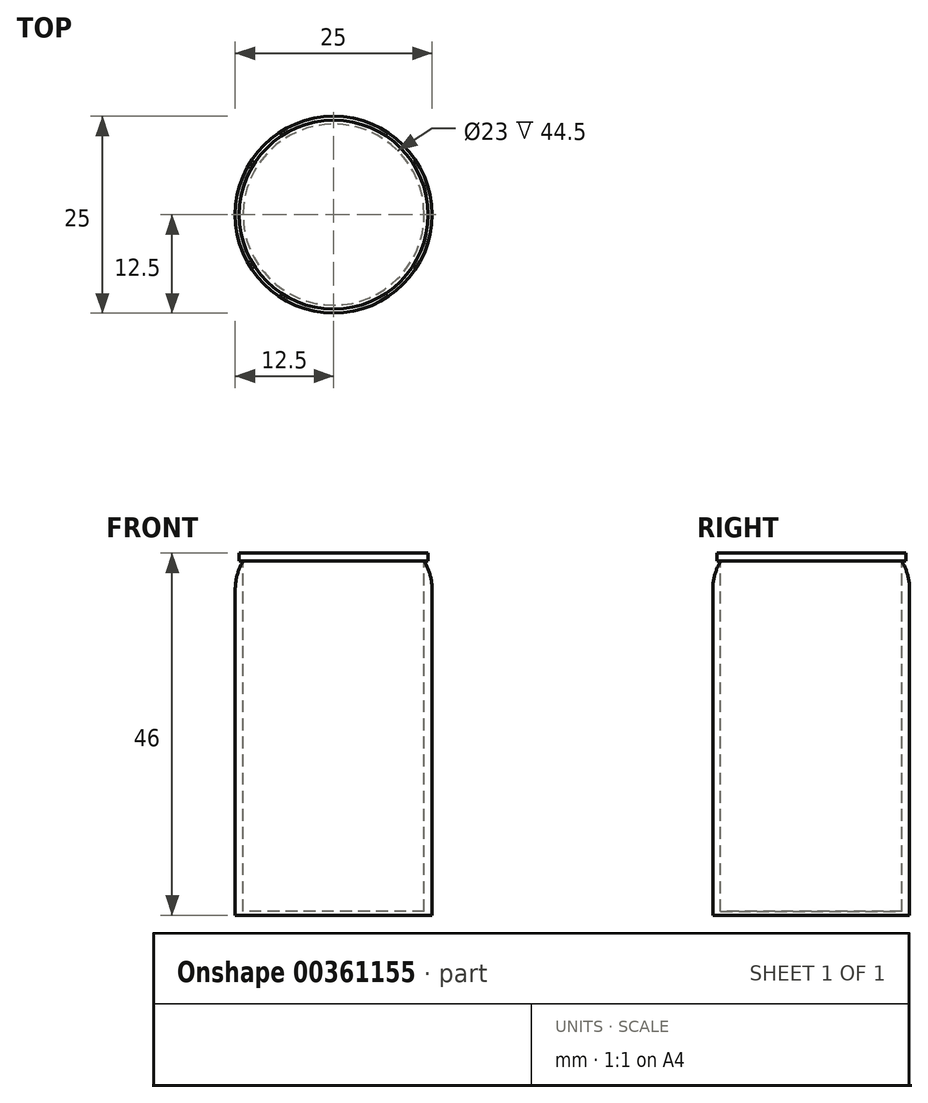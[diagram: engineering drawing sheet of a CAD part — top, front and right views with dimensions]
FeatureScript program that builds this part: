
annotation { "Feature Type Name" : "Feature", "Feature Type Description" : "" }
export const myFeature = defineFeature(function(context is Context, id is Id, definition is map)
    precondition{}
    {
        {
            var Q0;
            Q0=qCreatedBy(makeId("Top.planeOp"),FACE);
            var sketch = newSketch(context, id + "F0", { "sketchPlane" : qUnion([Q0])});
            skCircle(sketch, "E0", {"center": v(0, 0) * mm, "radius": 12.5 * mm});
            skSolve(sketch);
        }
        {
            var Q0;
            Q0 = qSketchRegion(id + "F0", true);
            extrude(context, id + "F1", {"entities" : qUnion([Q0]), "depth" : 45 * mm});
        }
        {
            var Q0;
            Q0=makeQuery(id+"F1.opExtrude","CAP_FACE",FACE,{"disambiguationData":[OSD([sQuery(id+"F0.wireOp",EDGE,"E0")])],"isStart":false});
            var sketch = newSketch(context, id + "F2", { "sketchPlane" : qUnion([Q0])});
            skCircle(sketch, "E1", {"center": v(0, 0) * mm, "radius": 6.5 * mm});
            skSolve(sketch);
        }
        {
            var Q0;
            Q0=makeQuery(id+"F2.imprint","IMPRINT",FACE,{"disambiguationData":[TD([[makeQuery(id+"F2.imprint","IMPRINT",EDGE,{"derivedFrom":sQuery(id+"F2.wireOp",EDGE,"E1")}),-1.0]])]});
            var sketch = newSketch(context, id + "F3", { "sketchPlane" : qUnion([Q0])});
            skCircle(sketch, "E2", {"center": v(0, 0) * mm, "radius": 11.5 * mm});
            skSolve(sketch);
        }
        {
            var Q0;
            Q0=makeQuery(id+"F3.imprint","IMPRINT",FACE,{"disambiguationData":[TD([[makeQuery(id+"F3.imprint","IMPRINT",EDGE,{"derivedFrom":sQuery(id+"F3.wireOp",EDGE,"E2")}),1.0]])]});
            extrude(context, id + "F4", {"entities" : qUnion([Q0]), "operationType" : NewBodyOperationType.REMOVE, "oppositeDirection" : true, "depth" : 44.5 * mm});
        }
        {
            var Q0;
            Q0=makeQuery(id+"F1.opExtrude","CAP_EDGE",EDGE,{"disambiguationData":[OSD([sQuery(id+"F0.wireOp",EDGE,"E0")])],"isStart":false});
            fillet(context, id + "F5", {"entities" : qUnion([Q0]), "radius" : 7 * mm, "tangentPropagation" : true, "allowEdgeOverflow" : false});
        }
        {
            var Q0;
            Q0=makeQuery(id+"F2.imprint","IMPRINT",FACE,{"disambiguationData":[TD([[makeQuery(id+"F2.imprint","IMPRINT",EDGE,{"derivedFrom":sQuery(id+"F2.wireOp",EDGE,"E1")}),1.0]])]});
            extrude(context, id + "F6", {"entities" : qUnion([Q0]), "operationType" : NewBodyOperationType.REMOVE, "oppositeDirection" : true, "depth" : 44.5 * mm});
        }
        {
            var Q0;
            Q0=makeQuery(id+"F2.imprint","IMPRINT",FACE,{"disambiguationData":[TD([[makeQuery(id+"F2.imprint","IMPRINT",EDGE,{"derivedFrom":sQuery(id+"F2.wireOp",EDGE,"E1")}),-1.0]])]});
            var sketch = newSketch(context, id + "F7", { "sketchPlane" : qUnion([Q0])});
            skCircle(sketch, "E3", {"center": v(0, 0) * mm, "radius": 12 * mm});
            skSolve(sketch);
        }
        {
            var Q0;
            Q0 = qSketchRegion(id + "F7", true);
            extrude(context, id + "F8", {"entities" : qUnion([Q0]), "depth" : 1 * mm});
        }
    });
